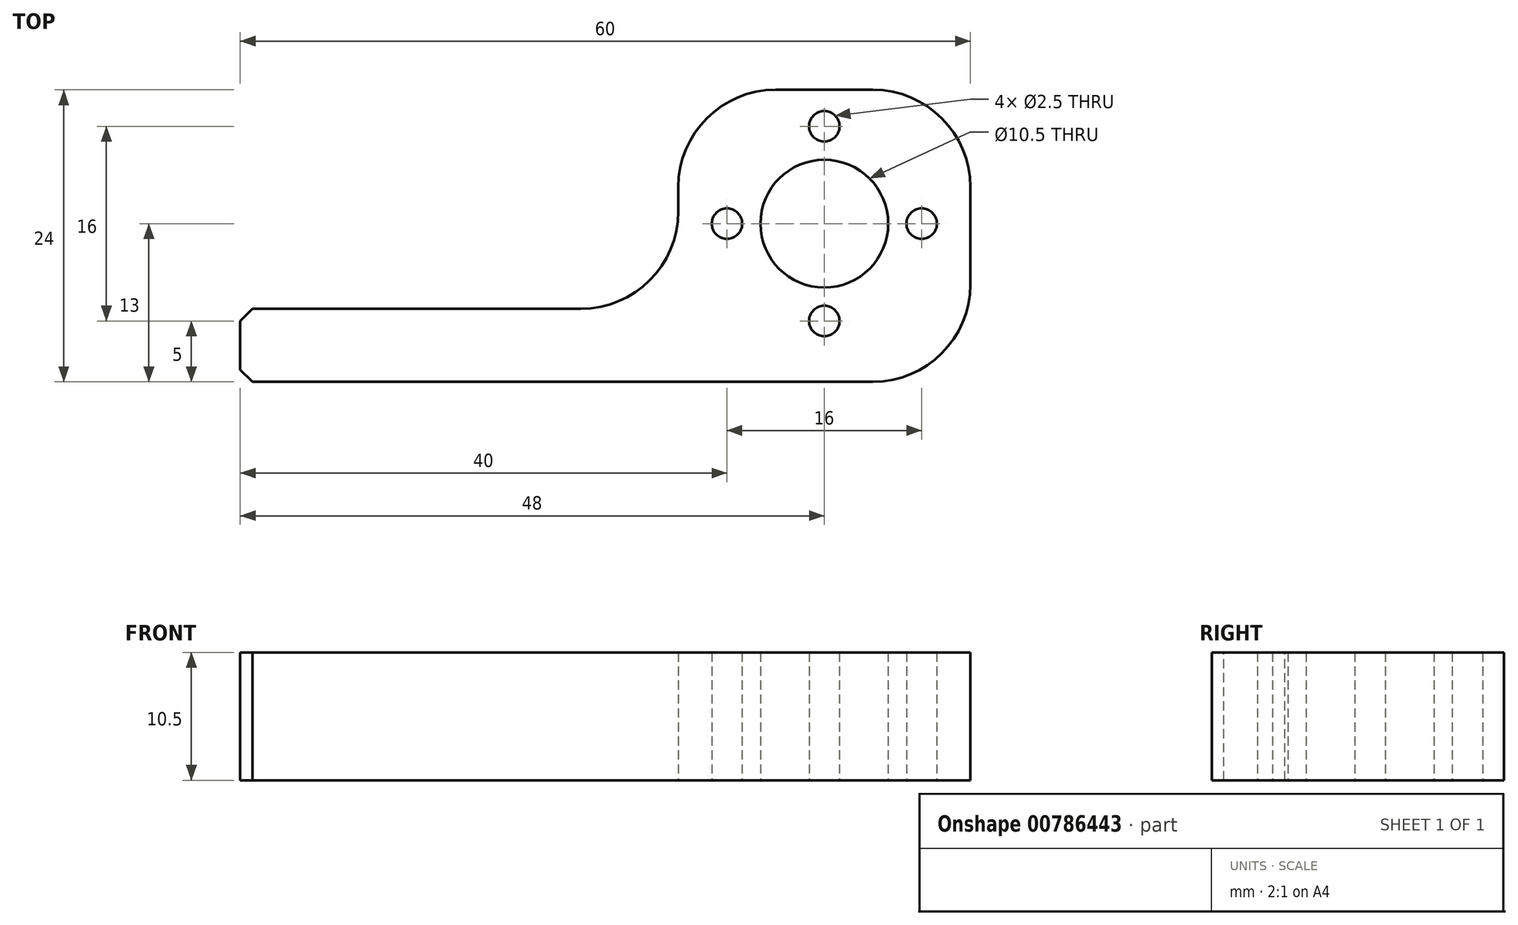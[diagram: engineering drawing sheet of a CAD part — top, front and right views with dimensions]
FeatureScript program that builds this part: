
annotation { "Feature Type Name" : "Feature", "Feature Type Description" : "" }
export const myFeature = defineFeature(function(context is Context, id is Id, definition is map)
    precondition{}
    {
        {
            var Q0;
            Q0=qCreatedBy(makeId("Top.planeOp"),FACE);
            var sketch = newSketch(context, id + "F0", { "sketchPlane" : qUnion([Q0])});
            skLineSegment(sketch, "E0", {"start": v(-12, -7) * mm, "end": v(-12, 11) * mm});
            skLineSegment(sketch, "E1", {"start": v(12, 11) * mm, "end": v(-12, 11) * mm});
            skLineSegment(sketch, "E2", {"start": v(12, -13) * mm, "end": v(12, 11) * mm});
            skLineSegment(sketch, "E3", {"start": v(-48, -7) * mm, "end": v(-48, -13) * mm});
            skLineSegment(sketch, "E4", {"start": v(-12, -7) * mm, "end": v(-48, -7) * mm});
            skLineSegment(sketch, "E5", {"start": v(-48, -13) * mm, "end": v(12, -13) * mm});
            skLineSegment(sketch, "E6", {"start": v(0, 13.18) * mm, "end": v(0, -15.76) * mm, "construction": true});
            skPoint(sketch, "E6.startSnap0", {"position": v(0, 11) * mm});
            skLineSegment(sketch, "E7", {"start": v(-19.15, 0) * mm, "end": v(18.99, 0) * mm, "construction": true});
            skPoint(sketch, "E8", {"position": v(-48, -10) * mm});
            skCircle(sketch, "E9", {"center": v(0, 0) * mm, "radius": 5.25 * mm});
            skCircle(sketch, "E10", {"center": v(0, 0) * mm, "radius": 11 * mm, "construction": true});
            skCircle(sketch, "E11", {"center": v(0, 0) * mm, "radius": 8 * mm, "construction": true});
            skCircle(sketch, "E12", {"center": v(-8, 0) * mm, "radius": 1.25 * mm});
            skCircle(sketch, "E13", {"center": v(0, 8) * mm, "radius": 1.25 * mm});
            skCircle(sketch, "E14", {"center": v(0, -8) * mm, "radius": 1.25 * mm});
            skCircle(sketch, "E15", {"center": v(8, 0) * mm, "radius": 1.25 * mm});
            skSolve(sketch);
        }
        {
            var Q0;
            Q0 = qSketchRegion(id + "F0", true);
            extrude(context, id + "F1", {"entities" : qUnion([Q0]), "depth" : 10.5 * mm, "offsetDistance" : 25 * mm});
        }
        {
            var Q0;
            Q0=makeQuery(id+"F1.opExtrude","SWEPT_EDGE",EDGE,{"disambiguationData":[OSD([sQuery(id+"F0.wireOp",EDGE,"E2"),sQuery(id+"F0.wireOp",EDGE,"E5")])]});
            var Q1;
            Q1=makeQuery(id+"F1.opExtrude","SWEPT_EDGE",EDGE,{"disambiguationData":[OSD([sQuery(id+"F0.wireOp",EDGE,"E1"),sQuery(id+"F0.wireOp",EDGE,"E2")])]});
            var Q2;
            Q2=makeQuery(id+"F1.opExtrude","SWEPT_EDGE",EDGE,{"disambiguationData":[OSD([sQuery(id+"F0.wireOp",EDGE,"E0"),sQuery(id+"F0.wireOp",EDGE,"E1")])]});
            var Q3;
            Q3=makeQuery(id+"F1.opExtrude","SWEPT_EDGE",EDGE,{"disambiguationData":[OSD([sQuery(id+"F0.wireOp",EDGE,"E0"),sQuery(id+"F0.wireOp",EDGE,"E4")])]});
            fillet(context, id + "F2", {"entities" : qUnion([Q0, Q1, Q2, Q3]), "radius" : 8 * mm, "tangentPropagation" : true, "allowEdgeOverflow" : false});
        }
        {
            var Q0;
            Q0=makeQuery(id+"F1.opExtrude","SWEPT_EDGE",EDGE,{"disambiguationData":[OSD([sQuery(id+"F0.wireOp",EDGE,"E3"),sQuery(id+"F0.wireOp",EDGE,"E5")])]});
            var Q1;
            Q1=makeQuery(id+"F1.opExtrude","SWEPT_EDGE",EDGE,{"disambiguationData":[OSD([sQuery(id+"F0.wireOp",EDGE,"E3"),sQuery(id+"F0.wireOp",EDGE,"E4")])]});
            chamfer(context, id + "F3", {"entities" : qUnion([Q0, Q1]), "width" : 1 * mm, "tangentPropagation" : true});
        }
    });
